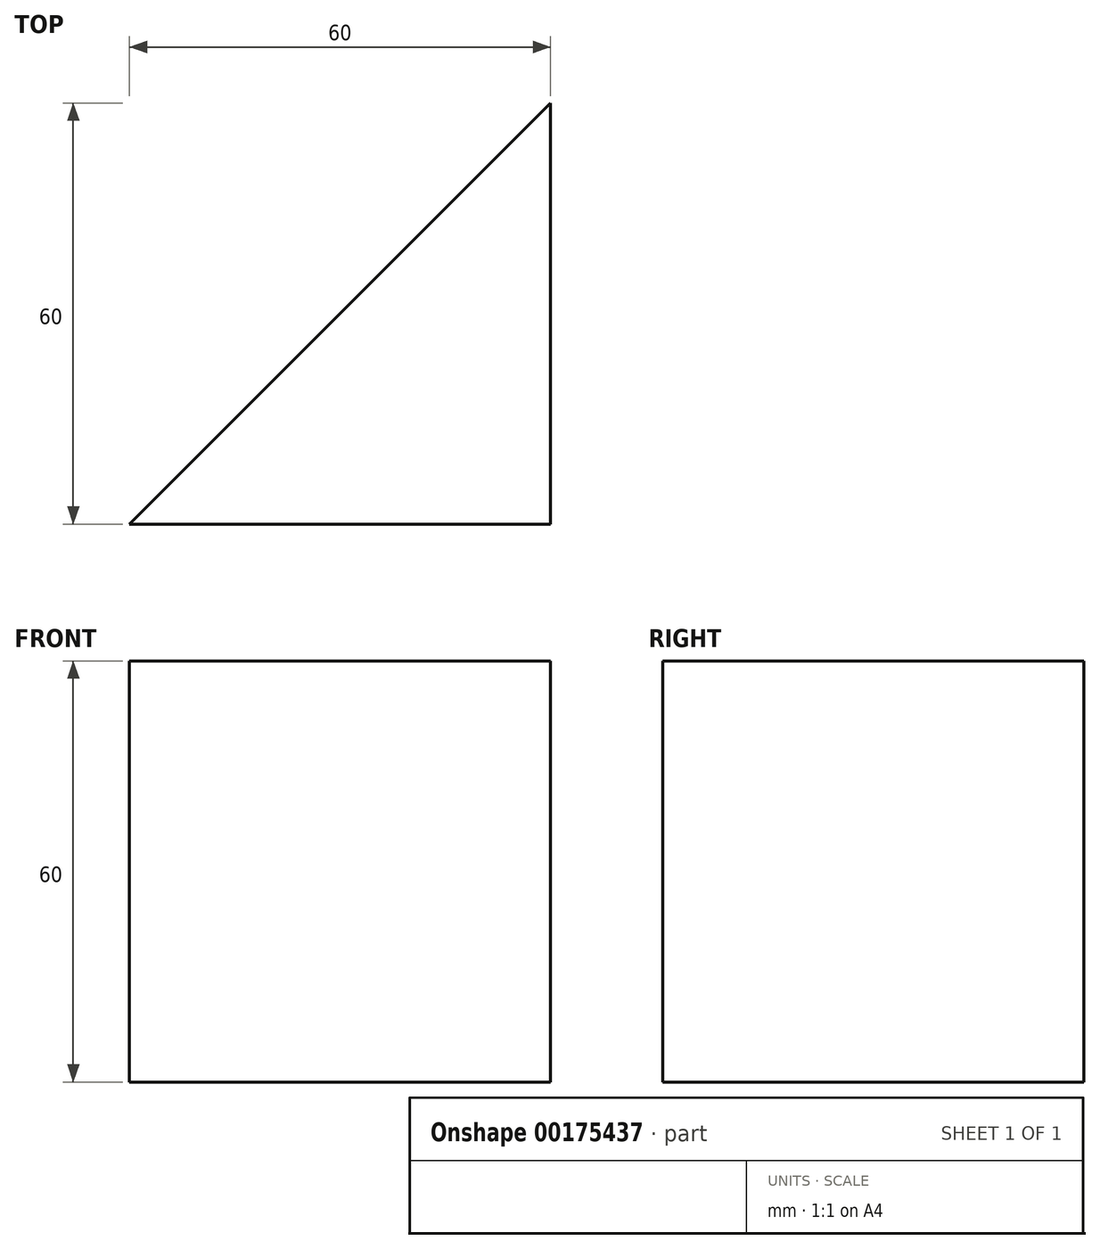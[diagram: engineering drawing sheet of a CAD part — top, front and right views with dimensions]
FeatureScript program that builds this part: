
annotation { "Feature Type Name" : "Feature", "Feature Type Description" : "" }
export const myFeature = defineFeature(function(context is Context, id is Id, definition is map)
    precondition{}
    {
        {
            var Q0;
            Q0=qCreatedBy(makeId("Top.planeOp"),FACE);
            var sketch = newSketch(context, id + "F0", { "sketchPlane" : qUnion([Q0])});
            skLineSegment(sketch, "E0.top", {"start": v(-17.37, -19.8) * mm, "end": v(42.63, -19.8) * mm});
            skLineSegment(sketch, "E0.right", {"start": v(42.63, 40.2) * mm, "end": v(42.63, -19.8) * mm});
            skLineSegment(sketch, "E1", {"start": v(-17.37, -19.8) * mm, "end": v(42.63, 40.2) * mm});
            skSolve(sketch);
        }
        {
            var Q0;
            Q0=makeQuery(id+"F0.imprint","IMPRINT",FACE,{"disambiguationData":[TD([[makeQuery(id+"F0.imprint","IMPRINT",EDGE,{"derivedFrom":sQuery(id+"F0.wireOp",EDGE,"E0.top")}),1.0]])]});
            extrude(context, id + "F1", {"entities" : qUnion([Q0]), "depth" : 60 * mm});
        }
    });
